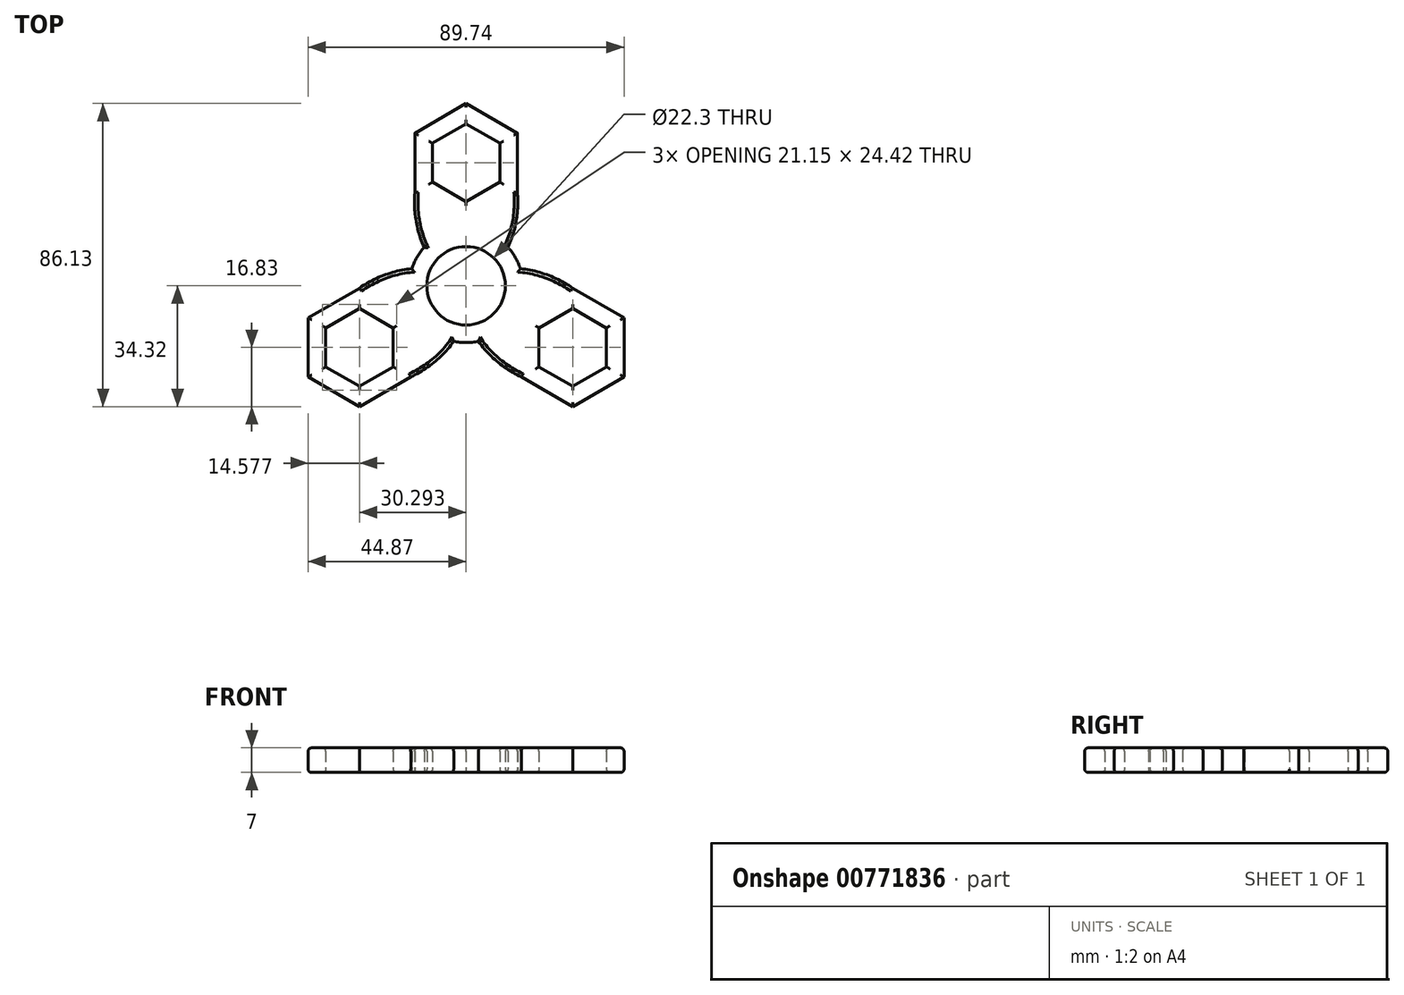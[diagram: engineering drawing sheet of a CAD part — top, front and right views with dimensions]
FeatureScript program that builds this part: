
annotation { "Feature Type Name" : "Feature", "Feature Type Description" : "" }
export const myFeature = defineFeature(function(context is Context, id is Id, definition is map)
    precondition{}
    {
        {
            var Q0;
            Q0=qCreatedBy(makeId("Top.planeOp"),FACE);
            var sketch = newSketch(context, id + "F0", { "sketchPlane" : qUnion([Q0])});
            skCircle(sketch, "E0", {"center": v(0, 0) * mm, "radius": 11.15 * mm});
            skCircle(sketch, "E1.0", {"center": v(0, 0) * mm, "radius": 16.15 * mm});
            skCircle(sketch, "E2.cCircle", {"center": v(0, 34.98) * mm, "radius": 11.06 * mm, "construction": true});
            skLineSegment(sketch, "E2.0", {"start": v(0, 23.92) * mm, "end": v(-9.57, 29.45) * mm});
            skLineSegment(sketch, "E2.1", {"start": v(-9.58, 29.45) * mm, "end": v(-9.58, 40.5) * mm});
            skLineSegment(sketch, "E2.2", {"start": v(-9.57, 40.5) * mm, "end": v(0, 46.04) * mm});
            skLineSegment(sketch, "E2.3", {"start": v(0, 46.04) * mm, "end": v(9.57, 40.5) * mm});
            skLineSegment(sketch, "E2.4", {"start": v(9.57, 40.5) * mm, "end": v(9.57, 29.45) * mm});
            skLineSegment(sketch, "E2.5", {"start": v(9.58, 29.45) * mm, "end": v(0, 23.92) * mm});
            skLineSegment(sketch, "E3.0", {"start": v(0, 51.8) * mm, "end": v(14.57, 43.4) * mm});
            skLineSegment(sketch, "E3.1", {"start": v(14.58, 26.56) * mm, "end": v(0, 18.15) * mm});
            skLineSegment(sketch, "E3.2", {"start": v(0, 18.15) * mm, "end": v(-14.58, 26.56) * mm});
            skLineSegment(sketch, "E3.3", {"start": v(14.57, 43.4) * mm, "end": v(14.57, 26.56) * mm});
            skLineSegment(sketch, "E3.4", {"start": v(-14.58, 26.56) * mm, "end": v(-14.58, 43.4) * mm});
            skLineSegment(sketch, "E3.5", {"start": v(-14.58, 43.4) * mm, "end": v(0, 51.8) * mm});
            skEllipse(sketch, "E4", {"center": v(0, 23.92) * mm, "majorRadius": 22.11 * mm, "minorRadius": 14.68 * mm, "majorAxis": v(0, 1)});
            skFitSpline(sketch, "E5.0", {"points": [v(1.4, 40.9) * mm, v(0, 41.1) * mm, v(-1.4, 40.9) * mm, v(-2.7, 40.33) * mm, v(-3.78, 39.56) * mm, v(-4.9, 38.56) * mm, v(-6.25, 36.9) * mm, v(-7.45, 34.71) * mm, v(-8.25, 32.69) * mm, v(-8.93, 30.53) * mm, v(-9.4, 28.2) * mm, v(-9.64, 25.78) * mm, v(-9.7, 23.92) * mm, v(-9.64, 22.07) * mm, v(-9.4, 19.65) * mm, v(-8.93, 17.32) * mm, v(-8.25, 15.16) * mm, v(-7.45, 13.13) * mm, v(-6.25, 10.95) * mm, v(-4.9, 9.29) * mm, v(-3.78, 8.29) * mm, v(-2.7, 7.52) * mm, v(-1.4, 6.95) * mm, v(0, 6.74) * mm, v(1.4, 6.95) * mm, v(2.7, 7.52) * mm, v(3.78, 8.29) * mm, v(4.9, 9.29) * mm, v(6.25, 10.95) * mm, v(7.45, 13.13) * mm, v(8.25, 15.16) * mm, v(8.93, 17.32) * mm, v(9.4, 19.65) * mm, v(9.64, 22.07) * mm, v(9.7, 23.92) * mm, v(9.64, 25.78) * mm, v(9.4, 28.2) * mm, v(8.93, 30.53) * mm, v(8.25, 32.69) * mm, v(7.45, 34.71) * mm, v(6.25, 36.9) * mm, v(4.9, 38.56) * mm, v(3.78, 39.56) * mm, v(2.7, 40.33) * mm, v(1.4, 40.9) * mm, v(0, 41.1) * mm, v(-1.4, 40.9) * mm, v(1.4, 40.9) * mm]});
            skSolve(sketch);
        }
        {
            var Q0;
            {var subQ0=sQuery(id+"F0.wireOp",EDGE,"UBTA8y4L-NzWo-JZS7-AoRI-JyAFkuAwjjts");var subQ1=sQuery(id+"F0.wireOp",EDGE,"E0");var subQ2=makeQuery(id+"F0.imprint","INTERSECT",VERTEX,{"disambiguationData":[OD(0.0)],"derivedFrom":[subQ1,subQ0]});Q0=makeQuery(id+"F0.imprint","IMPRINT",FACE,{"disambiguationData":[TD([[makeQuery(id+"F0.imprint","IMPRINT",EDGE,{"disambiguationData":[TD([[subQ2,-1.0]])],"derivedFrom":subQ1}),-1.0]])]});}
            var Q1;
            {var subQ0=sQuery(id+"F0.wireOp",EDGE,"8978ab03-5a34-4537-871f-21df63c45cd8.0");var subQ1=sQuery(id+"F0.wireOp",EDGE,"E0");var subQ2=makeQuery(id+"F0.imprint","INTERSECT",VERTEX,{"disambiguationData":[OD(0.0)],"derivedFrom":[subQ1,subQ0]});Q1=makeQuery(id+"F0.imprint","IMPRINT",FACE,{"disambiguationData":[TD([[makeQuery(id+"F0.imprint","IMPRINT",EDGE,{"disambiguationData":[TD([[subQ2,-1.0]])],"derivedFrom":subQ1}),-1.0]])]});}
            var Q2;
            {var subQ0=sQuery(id+"F0.wireOp",EDGE,"8978ab03-5a34-4537-871f-21df63c45cd8.0");var subQ1=sQuery(id+"F0.wireOp",EDGE,"E0");var subQ2=makeQuery(id+"F0.imprint","INTERSECT",VERTEX,{"disambiguationData":[OD(0.0)],"derivedFrom":[subQ1,subQ0]});Q2=makeQuery(id+"F0.imprint","IMPRINT",FACE,{"disambiguationData":[TD([[makeQuery(id+"F0.imprint","IMPRINT",EDGE,{"disambiguationData":[TD([[subQ2,1.0]])],"derivedFrom":subQ1}),-1.0]])]});}
            var Q3;
            {var subQ1=sQuery(id+"F0.wireOp",EDGE,"E3.0");Q3=makeQuery(id+"F0.imprint","IMPRINT",FACE,{"disambiguationData":[TD([[makeQuery(id+"F0.imprint","IMPRINT",EDGE,{"derivedFrom":subQ1}),1.0]])]});}
            var Q4;
            {var subQ0=sQuery(id+"F0.wireOp",EDGE,"8978ab03-5a34-4537-871f-21df63c45cd8.0");var subQ1=sQuery(id+"F0.wireOp",EDGE,"E0");var subQ2=makeQuery(id+"F0.imprint","INTERSECT",VERTEX,{"disambiguationData":[OD(1.0)],"derivedFrom":[subQ1,subQ0]});Q4=makeQuery(id+"F0.imprint","IMPRINT",FACE,{"disambiguationData":[TD([[makeQuery(id+"F0.imprint","IMPRINT",EDGE,{"disambiguationData":[TD([[subQ2,1.0]])],"derivedFrom":subQ1}),-1.0]])]});}
            var Q5;
            {var subQ1=sQuery(id+"F0.wireOp",EDGE,"E3.5");Q5=makeQuery(id+"F0.imprint","IMPRINT",FACE,{"disambiguationData":[TD([[makeQuery(id+"F0.imprint","IMPRINT",EDGE,{"derivedFrom":subQ1}),1.0]])]});}
            var Q6;
            Q6=makeQuery(id+"F0.imprint","IMPRINT",FACE,{"disambiguationData":[TD([[makeQuery(id+"F0.imprint","IMPRINT",EDGE,{"derivedFrom":sQuery(id+"F0.wireOp",EDGE,"E2.0")}),1.0]])]});
            var Q7;
            {var subQ0=sQuery(id+"F0.wireOp",EDGE,"8978ab03-5a34-4537-871f-21df63c45cd8.0");var subQ1=sQuery(id+"F0.wireOp",EDGE,"E0");var subQ2=makeQuery(id+"F0.imprint","INTERSECT",VERTEX,{"disambiguationData":[OD(1.0)],"derivedFrom":[subQ1,subQ0]});Q7=makeQuery(id+"F0.imprint","IMPRINT",FACE,{"disambiguationData":[TD([[makeQuery(id+"F0.imprint","IMPRINT",EDGE,{"disambiguationData":[TD([[subQ2,-1.0]])],"derivedFrom":subQ1}),-1.0]])]});}
            var Q8;
            {var subQ0=sQuery(id+"F0.wireOp",EDGE,"UBTA8y4L-NzWo-JZS7-AoRI-JyAFkuAwjjts");var subQ1=sQuery(id+"F0.wireOp",EDGE,"E0");var subQ2=makeQuery(id+"F0.imprint","INTERSECT",VERTEX,{"disambiguationData":[OD(0.0)],"derivedFrom":[subQ1,subQ0]});Q8=makeQuery(id+"F0.imprint","IMPRINT",FACE,{"disambiguationData":[TD([[makeQuery(id+"F0.imprint","IMPRINT",EDGE,{"disambiguationData":[TD([[subQ2,1.0]])],"derivedFrom":subQ1}),-1.0]])]});}
            var Q9;
            {var subQ0=sQuery(id+"F0.wireOp",EDGE,"HPvm7nAd-X5Sg-7byN-mMQC-0XuGKBpN7xoj");var subQ1=sQuery(id+"F0.wireOp",EDGE,"E1.0");var subQ2=makeQuery(id+"F0.imprint","INTERSECT",VERTEX,{"disambiguationData":[OD(0.0)],"derivedFrom":[subQ1,subQ0]});Q9=makeQuery(id+"F0.imprint","IMPRINT",FACE,{"disambiguationData":[TD([[makeQuery(id+"F0.imprint","IMPRINT",EDGE,{"disambiguationData":[TD([[subQ2,1.0]])],"derivedFrom":subQ1}),-1.0]])]});}
            var Q10;
            {var subQ0=sQuery(id+"F0.wireOp",EDGE,"HPvm7nAd-X5Sg-7byN-mMQC-0XuGKBpN7xoj");var subQ1=sQuery(id+"F0.wireOp",EDGE,"E1.0");var subQ2=makeQuery(id+"F0.imprint","INTERSECT",VERTEX,{"disambiguationData":[OD(1.0)],"derivedFrom":[subQ1,subQ0]});Q10=makeQuery(id+"F0.imprint","IMPRINT",FACE,{"disambiguationData":[TD([[makeQuery(id+"F0.imprint","IMPRINT",EDGE,{"disambiguationData":[TD([[subQ2,-1.0]])],"derivedFrom":subQ1}),-1.0]])]});}
            var Q11;
            {var subQ5=sQuery(id+"F0.wireOp",EDGE,"E2.5");var subQ6=sQuery(id+"F0.wireOp",EDGE,"E2.0");var subQ7=makeQuery(id+"F0.imprint","INTERSECT",VERTEX,{"derivedFrom":[subQ6,subQ5]});Q11=makeQuery(id+"F0.imprint","IMPRINT",FACE,{"disambiguationData":[TD([[makeQuery(id+"F0.imprint","IMPRINT",EDGE,{"disambiguationData":[TD([[subQ7,-1.0]])],"derivedFrom":subQ6}),1.0]])]});}
            var Q12;
            {var subQ1=sQuery(id+"F0.wireOp",EDGE,"E2.4");Q12=makeQuery(id+"F0.imprint","IMPRINT",FACE,{"disambiguationData":[TD([[makeQuery(id+"F0.imprint","IMPRINT",EDGE,{"derivedFrom":subQ1}),1.0]])]});}
            var Q13;
            {var subQ0=sQuery(id+"F0.wireOp",EDGE,"E4");var subQ1=sQuery(id+"F0.wireOp",EDGE,"E1.0");var subQ2=makeQuery(id+"F0.imprint","INTERSECT",VERTEX,{"disambiguationData":[OD(0.0)],"derivedFrom":[subQ1,subQ0]});Q13=makeQuery(id+"F0.imprint","IMPRINT",FACE,{"disambiguationData":[TD([[makeQuery(id+"F0.imprint","IMPRINT",EDGE,{"disambiguationData":[TD([[subQ2,-1.0]])],"derivedFrom":subQ1}),-1.0]])]});}
            var Q14;
            {var subQ0=sQuery(id+"F0.wireOp",EDGE,"E4");var subQ1=sQuery(id+"F0.wireOp",EDGE,"E1.0");var subQ2=makeQuery(id+"F0.imprint","INTERSECT",VERTEX,{"disambiguationData":[OD(1.0)],"derivedFrom":[subQ1,subQ0]});Q14=makeQuery(id+"F0.imprint","IMPRINT",FACE,{"disambiguationData":[TD([[makeQuery(id+"F0.imprint","IMPRINT",EDGE,{"disambiguationData":[TD([[subQ2,1.0]])],"derivedFrom":subQ1}),-1.0]])]});}
            var Q15;
            {var subQ0=sQuery(id+"F0.wireOp",EDGE,"E5.0");var subQ1=sQuery(id+"F0.wireOp",EDGE,"E0");var subQ2=makeQuery(id+"F0.imprint","INTERSECT",VERTEX,{"disambiguationData":[OD(1.0)],"derivedFrom":[subQ1,subQ0]});Q15=makeQuery(id+"F0.imprint","IMPRINT",FACE,{"disambiguationData":[TD([[makeQuery(id+"F0.imprint","IMPRINT",EDGE,{"disambiguationData":[TD([[subQ2,-1.0]])],"derivedFrom":subQ1}),-1.0]])]});}
            var Q16;
            {var subQ0=sQuery(id+"F0.wireOp",EDGE,"E5.0");var subQ1=sQuery(id+"F0.wireOp",EDGE,"E0");var subQ2=makeQuery(id+"F0.imprint","INTERSECT",VERTEX,{"disambiguationData":[OD(0.0)],"derivedFrom":[subQ1,subQ0]});Q16=makeQuery(id+"F0.imprint","IMPRINT",FACE,{"disambiguationData":[TD([[makeQuery(id+"F0.imprint","IMPRINT",EDGE,{"disambiguationData":[TD([[subQ2,1.0]])],"derivedFrom":subQ1}),-1.0]])]});}
            var Q17;
            {var subQ0=sQuery(id+"F0.wireOp",EDGE,"E4");var subQ1=sQuery(id+"F0.wireOp",EDGE,"E0");var subQ2=makeQuery(id+"F0.imprint","INTERSECT",VERTEX,{"disambiguationData":[OD(0.0)],"derivedFrom":[subQ1,subQ0]});Q17=makeQuery(id+"F0.imprint","IMPRINT",FACE,{"disambiguationData":[TD([[makeQuery(id+"F0.imprint","IMPRINT",EDGE,{"disambiguationData":[TD([[subQ2,1.0]])],"derivedFrom":subQ1}),-1.0]])]});}
            var Q18;
            {var subQ0=sQuery(id+"F0.wireOp",EDGE,"E5.0");var subQ1=sQuery(id+"F0.wireOp",EDGE,"E0");var subQ2=makeQuery(id+"F0.imprint","INTERSECT",VERTEX,{"disambiguationData":[OD(0.0)],"derivedFrom":[subQ1,subQ0]});Q18=makeQuery(id+"F0.imprint","IMPRINT",FACE,{"disambiguationData":[TD([[makeQuery(id+"F0.imprint","IMPRINT",EDGE,{"disambiguationData":[TD([[subQ2,-1.0]])],"derivedFrom":subQ1}),-1.0]])]});}
            var Q19;
            {var subQ0=sQuery(id+"F0.wireOp",EDGE,"E2.3");Q19=makeQuery(id+"F0.imprint","IMPRINT",FACE,{"disambiguationData":[TD([[makeQuery(id+"F0.imprint","IMPRINT",EDGE,{"derivedFrom":subQ0}),1.0]])]});}
            var Q20;
            {var subQ0=sQuery(id+"F0.wireOp",EDGE,"E2.2");Q20=makeQuery(id+"F0.imprint","IMPRINT",FACE,{"disambiguationData":[TD([[makeQuery(id+"F0.imprint","IMPRINT",EDGE,{"derivedFrom":subQ0}),1.0]])]});}
            var Q21;
            Q21=makeQuery(id+"F0.imprint","IMPRINT",FACE,{"disambiguationData":[TD([[makeQuery(id+"F0.imprint","IMPRINT",EDGE,{"derivedFrom":sQuery(id+"F0.wireOp",EDGE,"E3.0")}),-1.0]])]});
            extrude(context, id + "F1", {"entities" : qUnion([Q0, Q1, Q2, Q3, Q4, Q5, Q6, Q7, Q8, Q9, Q10, Q11, Q12, Q13, Q14, Q15, Q16, Q17, Q18, Q19, Q20, Q21]), "depth" : 7 * mm, "offsetDistance" : 25 * mm});
        }
        {
            var Q0;
            Q0=makeQuery(id+"F1.opExtrude","SWEPT_BODY",BODY,{"disambiguationData":[OSD([sQuery(id+"F0.wireOp",EDGE,"E0"),sQuery(id+"F0.wireOp",EDGE,"E1.0"),sQuery(id+"F0.wireOp",EDGE,"E2.0"),sQuery(id+"F0.wireOp",EDGE,"E2.1"),sQuery(id+"F0.wireOp",EDGE,"E2.2"),sQuery(id+"F0.wireOp",EDGE,"E2.3"),sQuery(id+"F0.wireOp",EDGE,"E2.4"),sQuery(id+"F0.wireOp",EDGE,"E2.5"),sQuery(id+"F0.wireOp",EDGE,"E3.1"),sQuery(id+"F0.wireOp",EDGE,"E3.2"),sQuery(id+"F0.wireOp",EDGE,"E3.3"),sQuery(id+"F0.wireOp",EDGE,"E3.4"),sQuery(id+"F0.wireOp",EDGE,"UBTA8y4L-NzWo-JZS7-AoRI-JyAFkuAwjjts"),sQuery(id+"F0.wireOp",EDGE,"8978ab03-5a34-4537-871f-21df63c45cd8.0")])]});
            var Q1;
            Q1=makeQuery(id+"F1.opExtrude","CAP_EDGE",EDGE,{"disambiguationData":[OSD([sQuery(id+"F0.wireOp",EDGE,"E0")])],"isStart":false});
            circularPattern(context, id + "F2", {"operationType" : NewBodyOperationType.ADD, "entities" : qUnion([Q0]), "axis" : qUnion([Q1]), "angle" : 360 * degree, "instanceCount" : 3, "equalSpace" : true});
        }
        {
            var Q0;
            {var subQ0=makeQuery(id+"F1.opExtrude","CAP_FACE",FACE,{"disambiguationData":[OSD([sQuery(id+"F0.wireOp",EDGE,"E0"),sQuery(id+"F0.wireOp",EDGE,"E1.0"),sQuery(id+"F0.wireOp",EDGE,"E2.0"),sQuery(id+"F0.wireOp",EDGE,"E2.1"),sQuery(id+"F0.wireOp",EDGE,"E2.2"),sQuery(id+"F0.wireOp",EDGE,"E2.3"),sQuery(id+"F0.wireOp",EDGE,"E2.4"),sQuery(id+"F0.wireOp",EDGE,"E2.5"),sQuery(id+"F0.wireOp",EDGE,"E3.1"),sQuery(id+"F0.wireOp",EDGE,"E3.2"),sQuery(id+"F0.wireOp",EDGE,"E3.3"),sQuery(id+"F0.wireOp",EDGE,"E3.4"),sQuery(id+"F0.wireOp",EDGE,"HPvm7nAd-X5Sg-7byN-mMQC-0XuGKBpN7xoj"),sQuery(id+"F0.wireOp",EDGE,"67dbe9c9-cc5a-4133-bc85-a2e3514c1358.0")])],"isStart":false});Q0=makeQuery(id+"F2.boolean.opBoolean","MERGE",FACE,{"derivedFrom":[subQ0,makeQuery(id+"F2.opPattern","COPY",FACE,{"derivedFrom":subQ0,"instanceName":"1"}),makeQuery(id+"F2.opPattern","COPY",FACE,{"derivedFrom":subQ0,"instanceName":"2"})]});}
            var Q1;
            {var subQ0=makeQuery(id+"F1.opExtrude","CAP_FACE",FACE,{"disambiguationData":[OSD([sQuery(id+"F0.wireOp",EDGE,"E0"),sQuery(id+"F0.wireOp",EDGE,"E1.0"),sQuery(id+"F0.wireOp",EDGE,"E2.0"),sQuery(id+"F0.wireOp",EDGE,"E2.1"),sQuery(id+"F0.wireOp",EDGE,"E2.2"),sQuery(id+"F0.wireOp",EDGE,"E2.3"),sQuery(id+"F0.wireOp",EDGE,"E2.4"),sQuery(id+"F0.wireOp",EDGE,"E2.5"),sQuery(id+"F0.wireOp",EDGE,"E3.1"),sQuery(id+"F0.wireOp",EDGE,"E3.2"),sQuery(id+"F0.wireOp",EDGE,"E3.3"),sQuery(id+"F0.wireOp",EDGE,"E3.4"),sQuery(id+"F0.wireOp",EDGE,"HPvm7nAd-X5Sg-7byN-mMQC-0XuGKBpN7xoj"),sQuery(id+"F0.wireOp",EDGE,"67dbe9c9-cc5a-4133-bc85-a2e3514c1358.0")])],"isStart":true});Q1=makeQuery(id+"F2.boolean.opBoolean","MERGE",FACE,{"derivedFrom":[subQ0,makeQuery(id+"F2.opPattern","COPY",FACE,{"derivedFrom":subQ0,"instanceName":"1"}),makeQuery(id+"F2.opPattern","COPY",FACE,{"derivedFrom":subQ0,"instanceName":"2"})]});}
            fillet(context, id + "F3", {"entities" : qUnion([Q0, Q1]), "radius" : 1 * mm, "tangentPropagation" : true, "allowEdgeOverflow" : false});
        }
    });
